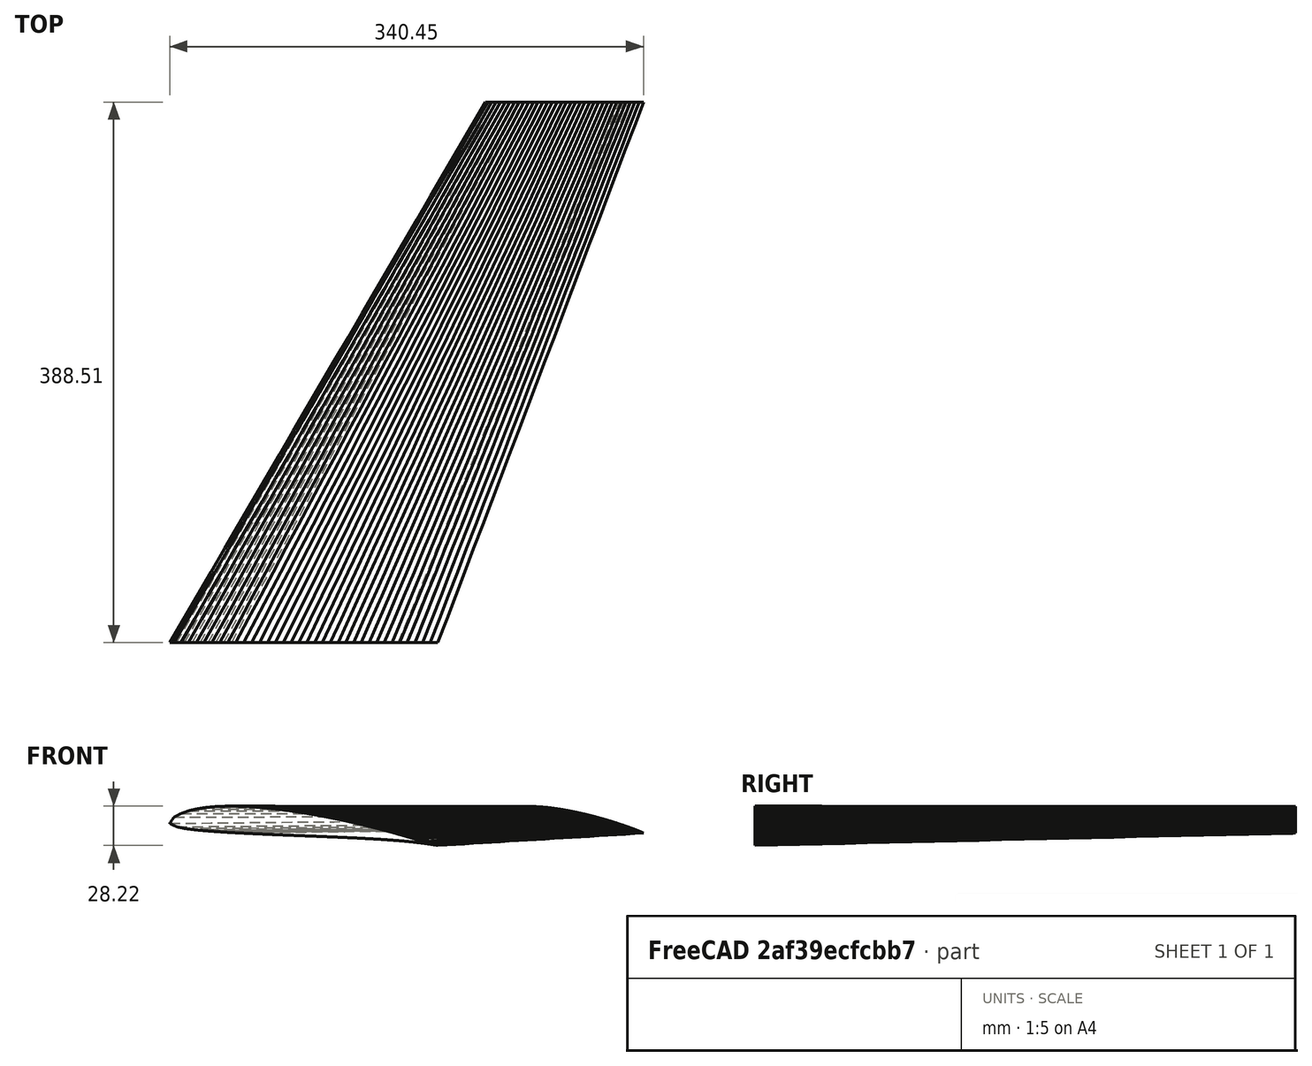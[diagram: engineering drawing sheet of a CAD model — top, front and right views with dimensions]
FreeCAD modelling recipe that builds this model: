
FCSTD DOCUMENT  (FreeCAD 1.0R39319 (Git))
Label: Wing
License: All rights reserved
LicenseURL: https://en.wikipedia.org/wiki/All_rights_reserved
objects: App::DocumentObjectGroup×3, Part::Part2DObjectPython×2, PartDesign::SubShapeBinder×2, Part::FeaturePython×2, Part::Loft×1, App::Part×1
note: 7 computed .brp shape members not serialized (recipe doc carries the construction recipe); baked Part::Feature solids carry a one-line shape summary decoded from their .brp
EXTERNAL_REF file=Spreadsheet.FCStd obj=plane

FEATURE [Part::Part2DObjectPython] Wire  # Draft 2D object (typed FeaturePython)
  Area = 0.0641761
  ChamferSize = 0
  Closed = true
  End = (0.970594,0.002256,0)
  FilletRadius = 0
  Length = 2.03286
  MakeFace = true
  Points = (69) [(1,0,0),(0.970931,0.004971,0),(0.941994,0.010676,0),(0.913096,0.016568,0),(0.884197,0.022463,0),(0.855281,0.028266,0),(0.826327,0.033885,0),+62 more]
  Start = (1,0,0)
  Subdivisions = 0
FEATURE [App::DocumentObjectGroup] sd7032
  Group = -> [Wire]
FEATURE [Part::Part2DObjectPython] Wire001  # Draft 2D object (typed FeaturePython)
  Area = 0.102817
  ChamferSize = 0
  Closed = true
  End = (0.969889,-0.002758,0)
  FilletRadius = 0
  Length = 2.06327
  MakeFace = true
  Points = (69) [(1,0,0),(0.971604,0.010359,0),(0.942895,0.018808,0),(0.914088,0.026914,0),(0.885187,0.034682,0),(0.856199,0.042118,0),(0.827128,0.049224,0),+62 more]
  Start = (1,0,0)
  Subdivisions = 0
FEATURE [App::DocumentObjectGroup] naca4415
  Group = -> [Wire001]
FEATURE [App::DocumentObjectGroup] Group  label="Airfoils Low Poly"
  Group = -> [sd7032,naca4415]
FEATURE [PartDesign::SubShapeBinder] Binder  label="Wing Base"
  BindCopyOnChange = 0
  BindMode = 0
  ClaimChildren = false
  Context = -> Part [Binder.]
  Fuse = false
  MakeFace = true
  OffsetFill = false
  OffsetIntersection = false
  OffsetJoinType = 0
  OffsetOpenResult = false
  PartialLoad = false
  Placement = pos=(0,0,0) rot=(1,0,0;1.5708rad)
  Refine = true
  Relative = true
  Support = -> [sd7032]
  _Version = 2
FEATURE [PartDesign::SubShapeBinder] Binder001  label="Wing Tip"
  BindCopyOnChange = 0
  BindMode = 0
  ClaimChildren = false
  Context = -> Part [Binder001.]
  Fuse = false
  MakeFace = true
  OffsetFill = false
  OffsetIntersection = false
  OffsetJoinType = 0
  OffsetOpenResult = false
  PartialLoad = false
  Placement = pos=(0,0,0) rot=(1,0,0;1.5708rad)
  Refine = true
  Relative = true
  Support = -> [naca4415]
  _Version = 2
FEATURE [Part::FeaturePython] Clone  label="Wing Base001"  # Draft clone (typed FeaturePython)
  AttacherType = Attacher::AttachEngine3D
  AttachmentOffset = pos=(48.5542,0,-120) rot=(0,0,1;-0.084525rad)
  AttachmentSupport = -> [XZ_Plane]
  Fuse = false
  MapMode = 5
  Objects = -> [Binder]
  Placement = pos=(48.5542,120,-2.66e-14) rot=(-0.998217,-0.042212,0.042212;4.7106rad)
  Scale = (193.508,193.508,1)
  expr: .AttachmentOffset.Base.x = <<Spreadsheet>>#plane.body_len * <<Spreadsheet>>#plane.wing_base_start * 1000
  expr: .AttachmentOffset.Base.y = <<Spreadsheet>>#plane.wing_lift * 1000 * <<Spreadsheet>>#plane.body_height
  expr: .AttachmentOffset.Base.z = -<<Spreadsheet>>#plane.body_span * 1000
  expr: .AttachmentOffset.Rotation.Angle = -<<Spreadsheet>>#plane.attack_angle
  expr: .Scale.x = <<Spreadsheet>>#plane.wing_chord * 1000
  expr: .Scale.y = <<Spreadsheet>>#plane.wing_chord * 1000 * <<Spreadsheet>>#plane.scale_y_wing_base
FEATURE [Part::FeaturePython] Clone001  label="Wing Tip001"  # Draft clone (typed FeaturePython)
  AttacherType = Attacher::AttachEngine3D
  AttachmentOffset = pos=(275.624,1.47756,-508.507) rot=(0,0,1;-0.078559rad)
  AttachmentSupport = -> [XZ_Plane]
  Fuse = false
  MapMode = 5
  Objects = -> [Binder001]
  Placement = pos=(275.624,508.507,1.47756) rot=(-0.998459,-0.039239,0.039239;4.71085rad)
  Scale = (113.823,113.823,1)
  expr: .AttachmentOffset.Base.x = <<Spreadsheet>>#plane.body_len * <<Spreadsheet>>#plane.wing_base_start * 1000 + sin(<<Spreadsheet>>#plane.sweep) * <<Spreadsheet>>#plane.leading_edge_length * 1000
  expr: .AttachmentOffset.Base.y = <<Spreadsheet>>#plane.wing_lift * 1000 * <<Spreadsheet>>#plane.body_height + sin(<<Spreadsheet>>#plane.dihedral) * <<Spreadsheet>>#plane.leading_edge_length * 1000
  expr: .AttachmentOffset.Base.z = -<<Spreadsheet>>#plane.body_span * 1000 - cos(<<Spreadsheet>>#plane.sweep) * cos(<<Spreadsheet>>#plane.dihedral) * <<Spreadsheet>>#plane.leading_edge_length * 1000
  expr: .AttachmentOffset.Rotation.Angle = -<<Spreadsheet>>#plane.attack_angle - <<Spreadsheet>>#plane.washout
  expr: .Scale.x = <<Spreadsheet>>#plane.wing_chord * 1000 * <<Spreadsheet>>#plane.taper_ratio
  expr: .Scale.y = <<Spreadsheet>>#plane.wing_chord * <<Spreadsheet>>#plane.taper_ratio * <<Spreadsheet>>#plane.scale_y_wing_tip * 1000
FEATURE [Part::Loft] Loft
  Closed = false
  MaxDegree = 5
  Ruled = true
  Sections = -> [Clone,Clone001]
  Solid = true
FEATURE [App::Part] Part
  Group = -> [Wire,Wire001,naca4415,sd7032,Group,Binder,Binder001,Clone,Clone001,Loft]
  Origin = -> Origin
  expr: .Placement.Base.x = 0
  expr: .Placement.Base.y = 0
  expr: .Placement.Base.z = 0
